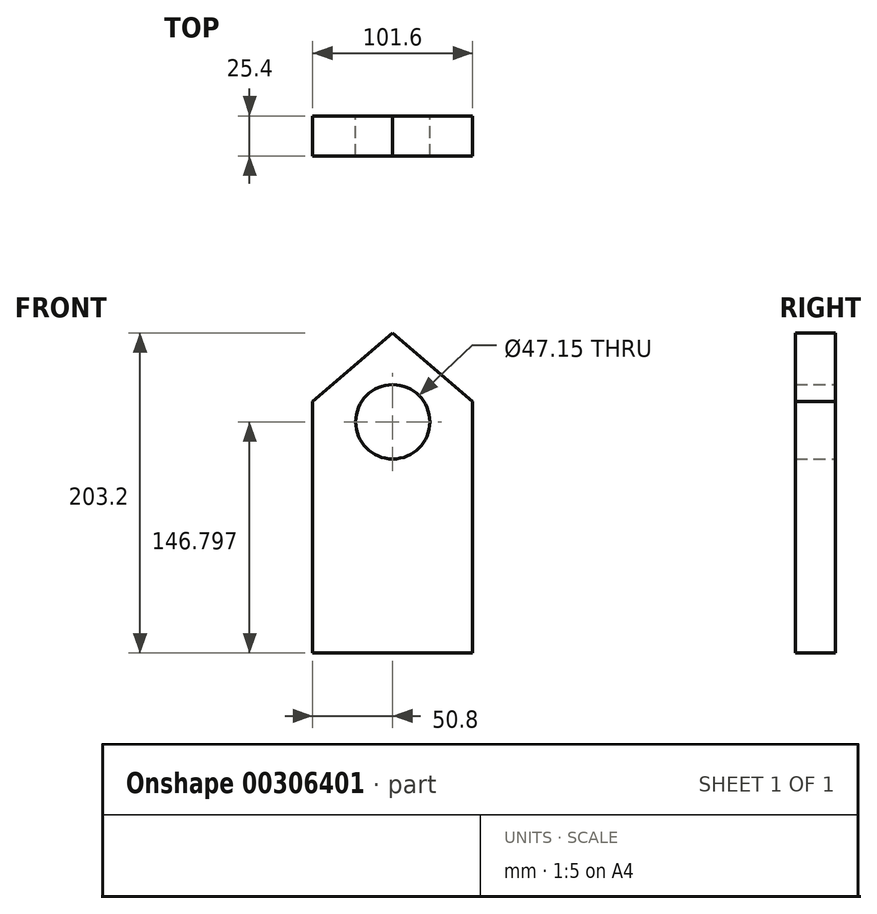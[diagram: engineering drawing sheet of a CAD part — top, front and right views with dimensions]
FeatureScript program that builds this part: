
annotation { "Feature Type Name" : "Feature", "Feature Type Description" : "" }
export const myFeature = defineFeature(function(context is Context, id is Id, definition is map)
    precondition{}
    {
        {
            var Q0;
            Q0=qCreatedBy(makeId("Front.planeOp"),FACE);
            var sketch = newSketch(context, id + "F0", { "sketchPlane" : qUnion([Q0])});
            skLineSegment(sketch, "E0.bottom", {"start": v(50.8, -101.6) * mm, "end": v(-50.8, -101.6) * mm});
            skLineSegment(sketch, "E0.top", {"start": v(50.8, 101.6) * mm, "end": v(-50.8, 101.6) * mm});
            skLineSegment(sketch, "E0.left", {"start": v(50.8, -101.6) * mm, "end": v(50.8, 101.6) * mm});
            skLineSegment(sketch, "E0.right", {"start": v(-50.8, -101.6) * mm, "end": v(-50.8, 101.6) * mm});
            skPoint(sketch, "E0.middle", {"position": v(0, 0) * mm});
            skLineSegment(sketch, "E1", {"start": v(-50.8, 58.03) * mm, "end": v(0, 101.6) * mm});
            skLineSegment(sketch, "E2", {"start": v(0, 101.6) * mm, "end": v(50.8, 58.03) * mm});
            skCircle(sketch, "E3", {"center": v(0, 45.2) * mm, "radius": 23.57 * mm});
            skSolve(sketch);
        }
        {
            var Q0;
            {var subQ2=sQuery(id+"F0.wireOp",EDGE,"E0.bottom");Q0=makeQuery(id+"F0.imprint","IMPRINT",FACE,{"disambiguationData":[TD([[makeQuery(id+"F0.imprint","IMPRINT",EDGE,{"derivedFrom":subQ2}),-1.0]])]});}
            extrude(context, id + "F1", {"entities" : qUnion([Q0]), "depth" : 25.4 * mm});
        }
    });
